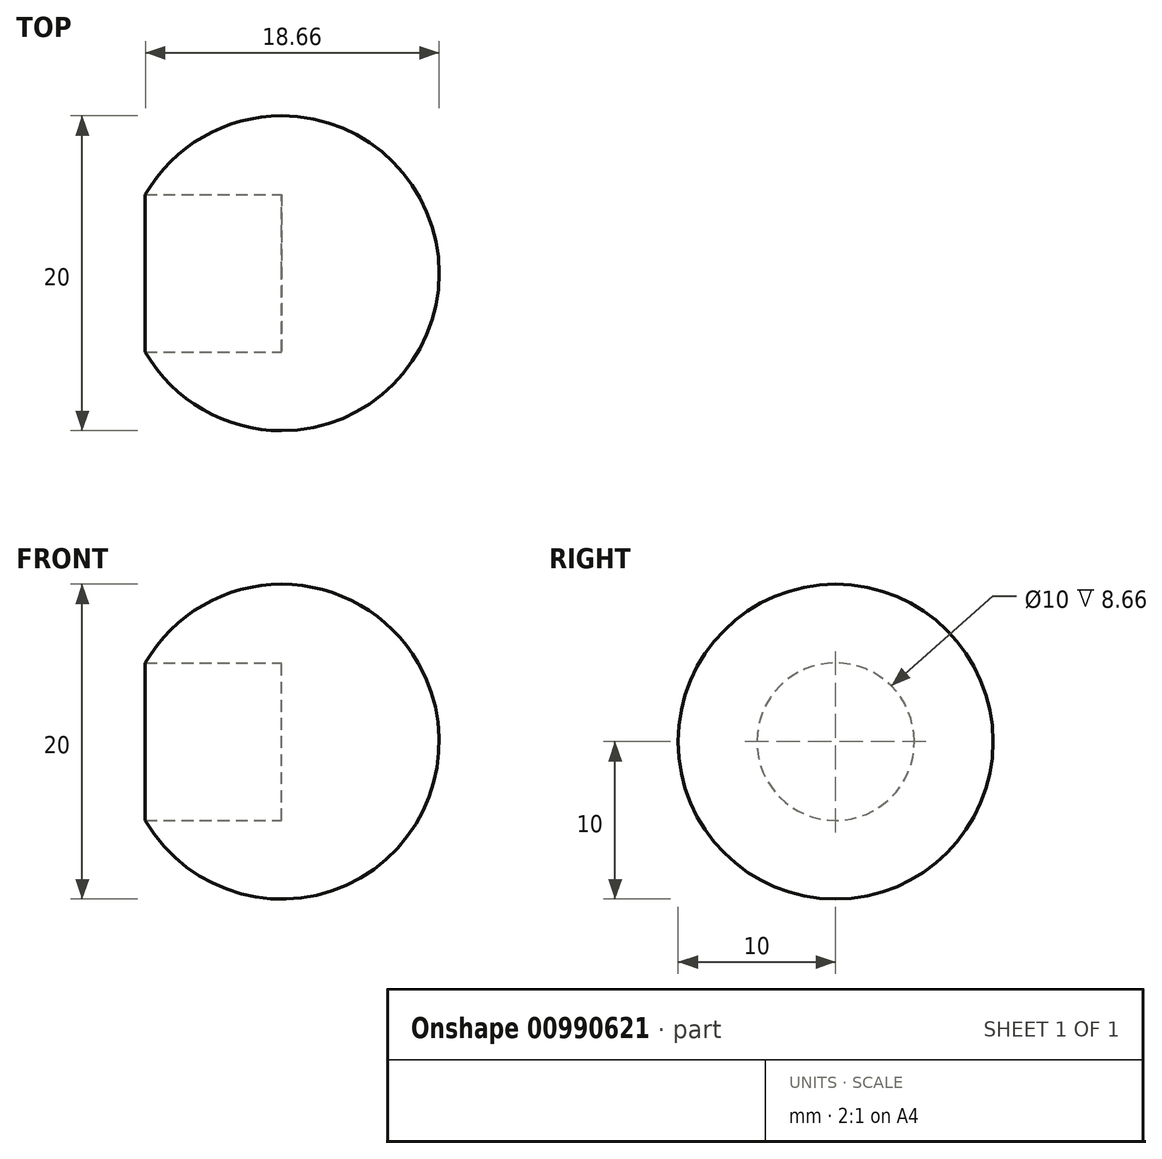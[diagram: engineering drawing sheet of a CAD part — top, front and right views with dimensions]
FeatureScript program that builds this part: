
annotation { "Feature Type Name" : "Feature", "Feature Type Description" : "" }
export const myFeature = defineFeature(function(context is Context, id is Id, definition is map)
    precondition{}
    {
        {
            var Q0;
            Q0=qCreatedBy(makeId("Right.planeOp"),FACE);
            var sketch = newSketch(context, id + "F0", { "sketchPlane" : qUnion([Q0])});
            skCircle(sketch, "E0", {"center": v(0, 0) * mm, "radius": 5 * mm});
            skSolve(sketch);
        }
        {
            var Q0;
            Q0=qCreatedBy(makeId("Right.planeOp"),FACE);
            var sketch = newSketch(context, id + "F1", { "sketchPlane" : qUnion([Q0])});
            skCircle(sketch, "E1", {"center": v(0, 0) * mm, "radius": 10 * mm});
            skSolve(sketch);
        }
        {
            var Q0;
            Q0=qCreatedBy(makeId("Front.planeOp"),FACE);
            var sketch = newSketch(context, id + "F2", { "sketchPlane" : qUnion([Q0])});
            skCircle(sketch, "E2", {"center": v(0, 0) * mm, "radius": 10 * mm});
            skSolve(sketch);
        }
        {
            var Q0;
            Q0=makeQuery(id+"F1.imprint","IMPRINT",FACE,{"disambiguationData":[TD([[makeQuery(id+"F1.imprint","IMPRINT",EDGE,{"derivedFrom":sQuery(id+"F1.wireOp",EDGE,"E1")}),1.0]])]});
            var Q1;
            Q1=sQuery(id+"F2.wireOp",EDGE,"E2");
            sweep(context, id + "F3", {"profiles" : qUnion([Q0]), "path" : qUnion([Q1])});
        }
        {
            var Q0;
            Q0 = qSketchRegion(id + "F0", true);
            extrude(context, id + "F4", {"entities" : qUnion([Q0]), "operationType" : NewBodyOperationType.REMOVE, "endBound" : BoundingType.THROUGH_ALL, "oppositeDirection" : true, "depth" : 25 * mm, "offsetDistance" : 25 * mm});
        }
    });
